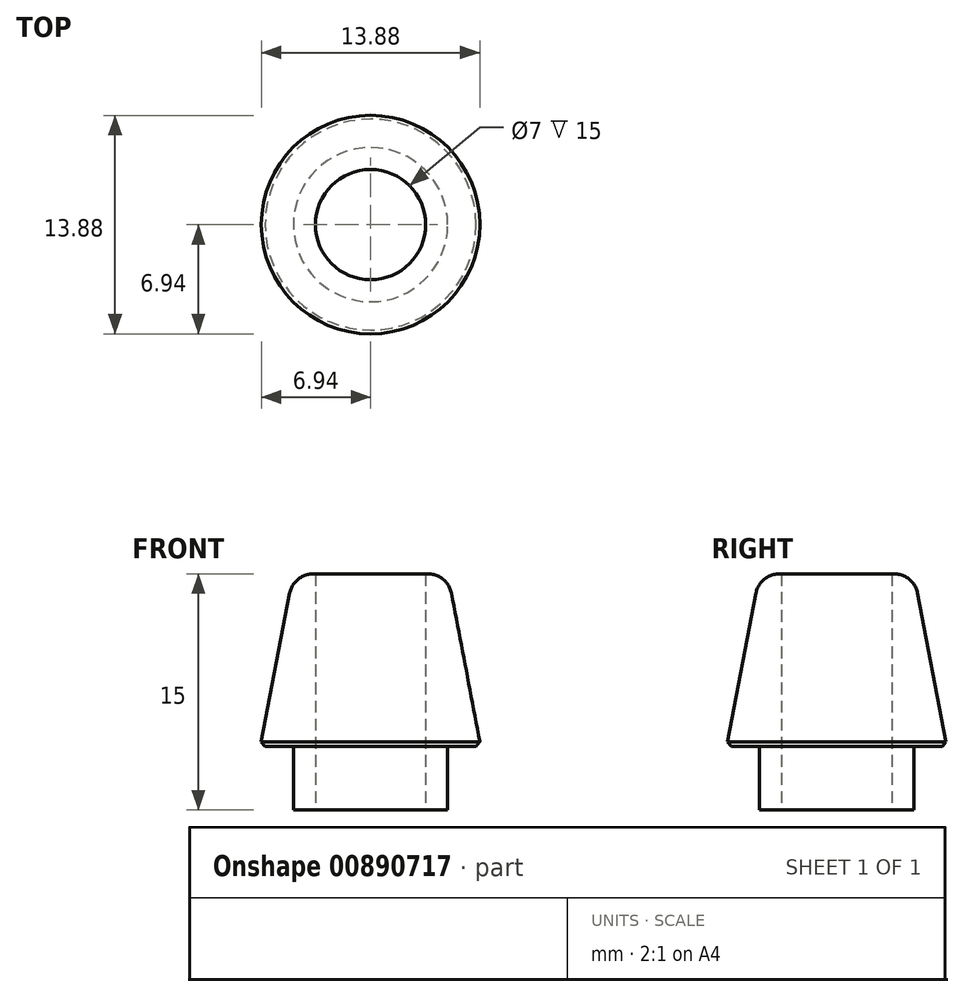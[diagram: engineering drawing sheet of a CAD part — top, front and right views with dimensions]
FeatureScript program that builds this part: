
annotation { "Feature Type Name" : "Feature", "Feature Type Description" : "" }
export const myFeature = defineFeature(function(context is Context, id is Id, definition is map)
    precondition{}
    {
        {
            var Q0;
            Q0=qCreatedBy(makeId("Front.planeOp"),FACE);
            var sketch = newSketch(context, id + "F0", { "sketchPlane" : qUnion([Q0])});
            skLineSegment(sketch, "E0", {"start": v(0, 0) * mm, "end": v(0, 15) * mm, "construction": true});
            skLineSegment(sketch, "E1", {"start": v(3.5, 0) * mm, "end": v(3.5, 15) * mm});
            skLineSegment(sketch, "E2", {"start": v(3.5, 15) * mm, "end": v(4.9, 15) * mm});
            skLineSegment(sketch, "E3", {"start": v(4.9, 15) * mm, "end": v(7, 4.05) * mm});
            skLineSegment(sketch, "E4", {"start": v(7, 4.05) * mm, "end": v(4.9, 4.05) * mm});
            skLineSegment(sketch, "E5", {"start": v(4.9, 4.05) * mm, "end": v(4.9, 0) * mm});
            skLineSegment(sketch, "E6", {"start": v(4.9, 0) * mm, "end": v(3.5, 0) * mm});
            skSolve(sketch);
        }
        {
            var Q0;
            Q0=makeQuery(id+"F0.imprint","IMPRINT",FACE,{"disambiguationData":[TD([[makeQuery(id+"F0.imprint","IMPRINT",EDGE,{"derivedFrom":sQuery(id+"F0.wireOp",EDGE,"E1")}),-1.0]])]});
            var Q1;
            Q1=sQuery(id+"F0.wireOp",EDGE,"E0");
            revolve(context, id + "F1", {"surfaceOperationType" : NewSurfaceOperationType.NEW, "entities" : qUnion([Q0]), "axis" : qUnion([Q1]), "revolveType" : RevolveType.FULL});
        }
        {
            var Q0;
            Q0=makeQuery(id+"F1.opRevolve","SWEPT_EDGE",EDGE,{"disambiguationData":[OSD([sQuery(id+"F0.wireOp",EDGE,"E2"),sQuery(id+"F0.wireOp",EDGE,"E3")])]});
            fillet(context, id + "F2", {"entities" : qUnion([Q0]), "radius" : 1.5 * mm, "tangentPropagation" : true, "allowEdgeOverflow" : false});
        }
        {
            var Q0;
            Q0=makeQuery(id+"F1.opRevolve","SWEPT_EDGE",EDGE,{"disambiguationData":[OSD([sQuery(id+"F0.wireOp",EDGE,"E3"),sQuery(id+"F0.wireOp",EDGE,"E4")])]});
            chamfer(context, id + "F3", {"entities" : qUnion([Q0]), "width" : .25 * mm, "tangentPropagation" : true});
        }
    });
